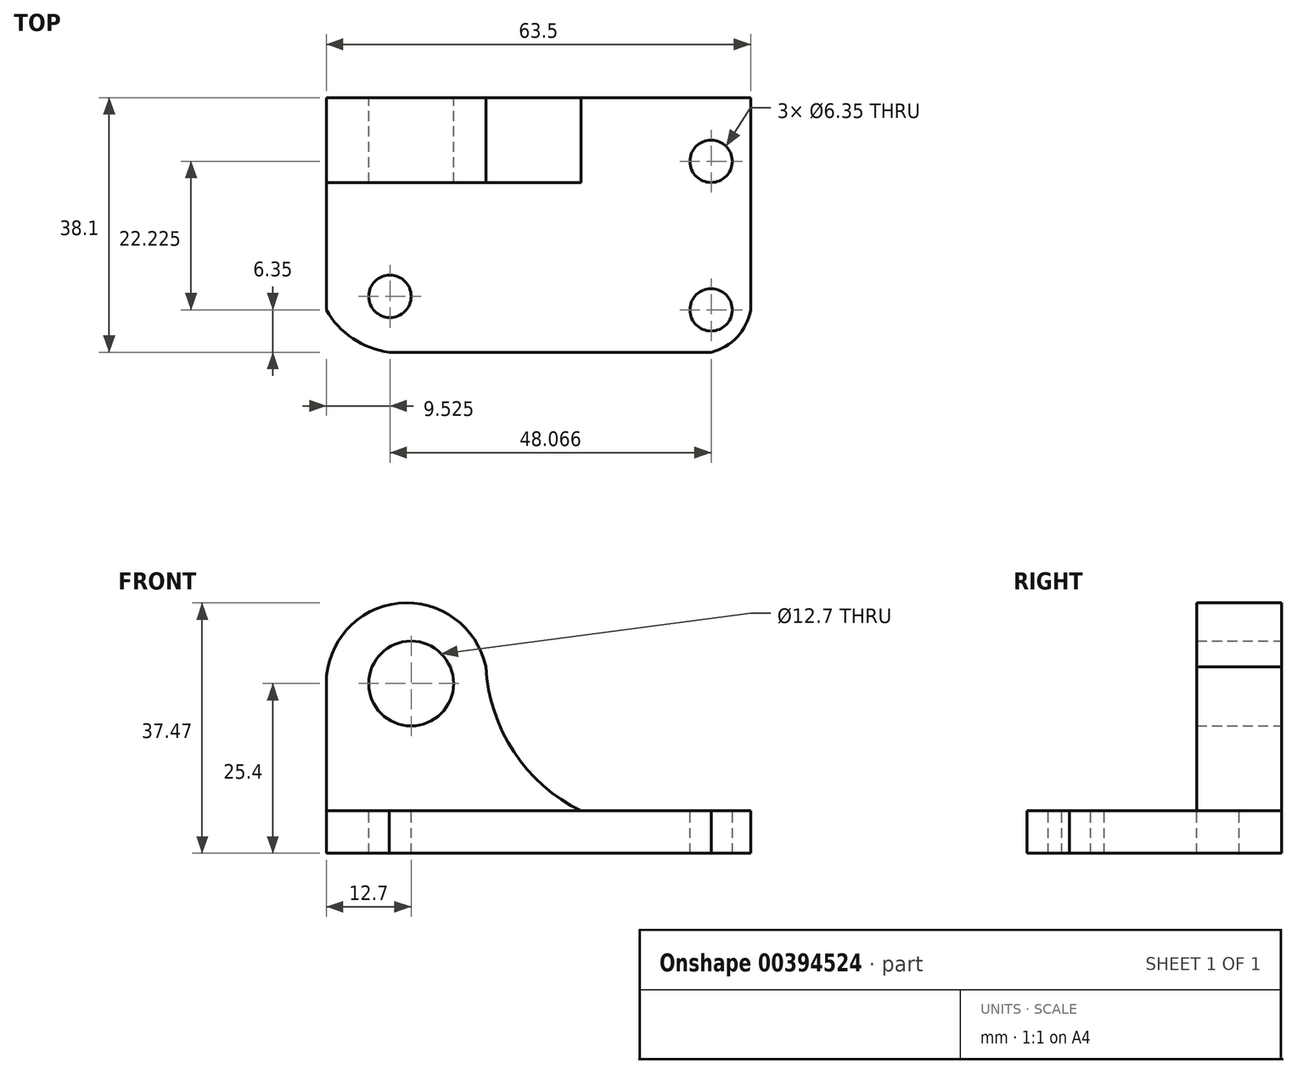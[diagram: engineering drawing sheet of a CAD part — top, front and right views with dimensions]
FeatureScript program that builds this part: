
annotation { "Feature Type Name" : "Feature", "Feature Type Description" : "" }
export const myFeature = defineFeature(function(context is Context, id is Id, definition is map)
    precondition{}
    {
        {
            var Q0;
            Q0=qCreatedBy(makeId("Front.planeOp"),FACE);
            var sketch = newSketch(context, id + "F0", { "sketchPlane" : qUnion([Q0])});
            skLineSegment(sketch, "E0", {"start": v(0, 0) * mm, "end": v(63.5, 0) * mm});
            skLineSegment(sketch, "E1", {"start": v(63.5, 0) * mm, "end": v(63.5, 6.35) * mm});
            skLineSegment(sketch, "E2", {"start": v(63.5, 6.35) * mm, "end": v(38.1, 6.35) * mm});
            skLineSegment(sketch, "E3", {"start": v(38.1, 6.35) * mm, "end": v(38.1, 38.1) * mm});
            skLineSegment(sketch, "E4", {"start": v(38.1, 38.1) * mm, "end": v(0, 38.1) * mm});
            skLineSegment(sketch, "E5", {"start": v(0, 38.1) * mm, "end": v(0, 0) * mm});
            skSolve(sketch);
        }
        {
            var Q0;
            Q0 = qSketchRegion(id + "F0", true);
            extrude(context, id + "F1", {"entities" : qUnion([Q0]), "depth" : 38.1 * mm});
        }
        {
            var Q0;
            Q0=qCreatedBy(makeId("Front.planeOp"),FACE);
            var sketch = newSketch(context, id + "F2", { "sketchPlane" : qUnion([Q0])});
            skArc(sketch, "E6", {"start": v(25.4, 38.1) * mm, "mid": v(25.66, 19.8) * mm, "end": v(38.1, 6.35) * mm});
            skLineSegment(sketch, "E7", {"start": v(38.1, 6.35) * mm, "end": v(38.1, 38.1) * mm});
            skLineSegment(sketch, "E8", {"start": v(25.4, 38.1) * mm, "end": v(38.1, 38.1) * mm});
            skSolve(sketch);
        }
        {
            var Q0;
            Q0 = qSketchRegion(id + "F2", true);
            extrude(context, id + "F3", {"entities" : qUnion([Q0]), "operationType" : NewBodyOperationType.REMOVE, "depth" : 38.1 * mm});
        }
        {
            var Q0;
            Q0=qCreatedBy(makeId("Front.planeOp"),FACE);
            var sketch = newSketch(context, id + "F4", { "sketchPlane" : qUnion([Q0])});
            skCircle(sketch, "E9", {"center": v(12.7, 25.4) * mm, "radius": 6.35 * mm});
            skSolve(sketch);
        }
        {
            var Q0;
            Q0 = qSketchRegion(id + "F4", true);
            extrude(context, id + "F5", {"entities" : qUnion([Q0]), "operationType" : NewBodyOperationType.REMOVE, "depth" : 38.1 * mm});
        }
        {
            var Q0;
            Q0=makeQuery(id+"F1.opExtrude","CAP_FACE",FACE,{"disambiguationData":[OSD([sQuery(id+"F0.wireOp",EDGE,"E0"),sQuery(id+"F0.wireOp",EDGE,"E1"),sQuery(id+"F0.wireOp",EDGE,"E2"),sQuery(id+"F0.wireOp",EDGE,"E3"),sQuery(id+"F0.wireOp",EDGE,"E4"),sQuery(id+"F0.wireOp",EDGE,"E5")])],"isStart":false});
            var sketch = newSketch(context, id + "F6", { "sketchPlane" : qUnion([Q0])});
            skArc(sketch, "E10", {"start": v(24.13, 25.4) * mm, "mid": v(12.07, 37.47) * mm, "end": v(0, 25.4) * mm});
            skSolve(sketch);
        }
        {
            var Q0;
            {var subQ5=makeQuery(id+"F1.opExtrude","CAP_EDGE",EDGE,{"disambiguationData":[OSD([sQuery(id+"F0.wireOp",EDGE,"E4")])],"isStart":false});Q0=makeQuery(id+"F6.imprint","IMPRINT",FACE,{"disambiguationData":[TD([[makeQuery(id+"F6.imprint","IMPRINT",EDGE,{"derivedFrom":subQ5}),1.0]])]});}
            extrude(context, id + "F7", {"entities" : qUnion([Q0]), "operationType" : NewBodyOperationType.REMOVE, "oppositeDirection" : true, "depth" : 38.1 * mm});
        }
        {
            var Q0;
            Q0=makeQuery(id+"F1.opExtrude","SWEPT_FACE",FACE,{"disambiguationData":[OSD([sQuery(id+"F0.wireOp",EDGE,"E2")])]});
            var sketch = newSketch(context, id + "F8", { "sketchPlane" : qUnion([Q0])});
            skLineSegment(sketch, "E11", {"start": v(0, -37.95) * mm, "end": v(0, -12.7) * mm});
            skLineSegment(sketch, "E12", {"start": v(0, -12.7) * mm, "end": v(38.1, -12.7) * mm});
            skLineSegment(sketch, "E13", {"start": v(38.1, -12.7) * mm, "end": v(38.1, -38.1) * mm});
            skLineSegment(sketch, "E14", {"start": v(38.1, -38.1) * mm, "end": v(0, -38.1) * mm});
            skLineSegment(sketch, "E15", {"start": v(0, -38.1) * mm, "end": v(0, -37.95) * mm});
            skSolve(sketch);
        }
        {
            var Q0;
            Q0 = qSketchRegion(id + "F8", true);
            extrude(context, id + "F9", {"entities" : qUnion([Q0]), "operationType" : NewBodyOperationType.REMOVE, "depth" : 31.75 * mm});
        }
        {
            var Q0;
            Q0=makeQuery(id+"F9.boolean.opBoolean","MERGE",FACE,{"derivedFrom":[makeQuery(id+"F1.opExtrude","SWEPT_FACE",FACE,{"disambiguationData":[OSD([sQuery(id+"F0.wireOp",EDGE,"E2")])]}),makeQuery(id+"F9.opExtrude","CAP_FACE",FACE,{"disambiguationData":[OSD([sQuery(id+"F8.wireOp",EDGE,"E11"),sQuery(id+"F8.wireOp",EDGE,"E12"),sQuery(id+"F8.wireOp",EDGE,"E13"),sQuery(id+"F8.wireOp",EDGE,"E14"),sQuery(id+"F8.wireOp",EDGE,"E15")])],"isStart":true})]});
            var sketch = newSketch(context, id + "F10", { "sketchPlane" : qUnion([Q0])});
            skArc(sketch, "E16", {"start": v(0, -31.75) * mm, "mid": v(5.38, -36.87) * mm, "end": v(12.7, -38.1) * mm});
            skLineSegment(sketch, "E17", {"start": v(0, -31.75) * mm, "end": v(0, -38.1) * mm});
            skLineSegment(sketch, "E18", {"start": v(0, -38.1) * mm, "end": v(12.7, -38.1) * mm});
            skSolve(sketch);
        }
        {
            var Q0;
            Q0 = qSketchRegion(id + "F10", true);
            extrude(context, id + "F11", {"entities" : qUnion([Q0]), "operationType" : NewBodyOperationType.REMOVE, "oppositeDirection" : true, "depth" : 25.4 * mm});
        }
        {
            var Q0;
            Q0=makeQuery(id+"F9.boolean.opBoolean","MERGE",FACE,{"derivedFrom":[makeQuery(id+"F1.opExtrude","SWEPT_FACE",FACE,{"disambiguationData":[OSD([sQuery(id+"F0.wireOp",EDGE,"E2")])]}),makeQuery(id+"F9.opExtrude","CAP_FACE",FACE,{"disambiguationData":[OSD([sQuery(id+"F8.wireOp",EDGE,"E11"),sQuery(id+"F8.wireOp",EDGE,"E12"),sQuery(id+"F8.wireOp",EDGE,"E13"),sQuery(id+"F8.wireOp",EDGE,"E14"),sQuery(id+"F8.wireOp",EDGE,"E15")])],"isStart":true})]});
            var sketch = newSketch(context, id + "F12", { "sketchPlane" : qUnion([Q0])});
            skArc(sketch, "E19", {"start": v(53.87, -38.1) * mm, "mid": v(60.07, -37.02) * mm, "end": v(63.5, -31.75) * mm});
            skLineSegment(sketch, "E20", {"start": v(63.5, -31.75) * mm, "end": v(63.5, -38.1) * mm});
            skLineSegment(sketch, "E21", {"start": v(63.5, -38.1) * mm, "end": v(53.87, -38.1) * mm});
            skSolve(sketch);
        }
        {
            var Q0;
            Q0 = qSketchRegion(id + "F12", true);
            extrude(context, id + "F13", {"entities" : qUnion([Q0]), "operationType" : NewBodyOperationType.REMOVE, "oppositeDirection" : true, "depth" : 25.4 * mm});
        }
        {
            var Q0;
            Q0=makeQuery(id+"F9.boolean.opBoolean","MERGE",FACE,{"derivedFrom":[makeQuery(id+"F1.opExtrude","SWEPT_FACE",FACE,{"disambiguationData":[OSD([sQuery(id+"F0.wireOp",EDGE,"E2")])]}),makeQuery(id+"F9.opExtrude","CAP_FACE",FACE,{"disambiguationData":[OSD([sQuery(id+"F8.wireOp",EDGE,"E11"),sQuery(id+"F8.wireOp",EDGE,"E12"),sQuery(id+"F8.wireOp",EDGE,"E13"),sQuery(id+"F8.wireOp",EDGE,"E14"),sQuery(id+"F8.wireOp",EDGE,"E15")])],"isStart":true})]});
            var sketch = newSketch(context, id + "F14", { "sketchPlane" : qUnion([Q0])});
            skCircle(sketch, "E22", {"center": v(9.53, -29.73) * mm, "radius": 3.18 * mm});
            skCircle(sketch, "E23", {"center": v(57.6, -31.75) * mm, "radius": 3.18 * mm});
            skCircle(sketch, "E24", {"center": v(57.6, -9.53) * mm, "radius": 3.18 * mm});
            skSolve(sketch);
        }
        {
            var Q0;
            Q0 = qSketchRegion(id + "F14", true);
            extrude(context, id + "F15", {"entities" : qUnion([Q0]), "operationType" : NewBodyOperationType.REMOVE, "oppositeDirection" : true, "depth" : 25.4 * mm});
        }
    });
